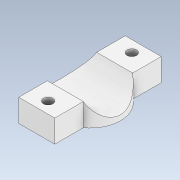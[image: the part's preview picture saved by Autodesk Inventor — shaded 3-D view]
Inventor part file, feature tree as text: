
AUTODESK INVENTOR PART (.ipt)
format: ipt  version: 2022 (Build 260153000, 153)  size: 269,312 bytes
history: native  units: mm
features: extrude x20, sketch x20, projected_geometry x15, plane x2
ambient origin geometry x8: Origin, YZ Plane, XZ Plane, XY Plane, X Axis, Y Axis, Z Axis, Center Point
bodies: Solid1 (feature_tree)
feature tree (57):
  extrude  "Extrusion1"  Depth=22.0mm
  extrude  "Extrusion2"  Depth=10.0mm
  extrude  "Extrusion3"  Depth=15.0mm
  extrude  "Extrusion4"  Depth=10.0mm TaperAngle=0.0deg
  extrude  "Extrusion5"  Depth=5.0mm
  extrude  "Extrusion6"  Depth=10.0mm
  plane  "Work Plane1"
  extrude  "Extrusion7"  Depth=29.0mm
  extrude  "Extrusion8"  TaperAngle=0.0deg  [1 undecoded]
  extrude  "Extrusion9"  Depth=10.0mm TaperAngle=0.0deg
  extrude  "Extrusion10"  TaperAngle=0.0deg  [1 undecoded]
  extrude  "Extrusion11"  Depth=10.0mm TaperAngle=0.0deg
  plane  "Work Plane2"
  extrude  "Extrusion12"  TaperAngle=0.0deg  [1 undecoded]
  extrude  "Extrusion13"  Depth=10.0mm TaperAngle=0.0deg
  extrude  "Extrusion14"  Depth=8.5mm
  extrude  "Extrusion15"  Depth=2.7mm TaperAngle=0.0deg
  extrude  "Extrusion16"  [1 undecoded]
  extrude  "Extrusion17"  [1 undecoded]
  extrude  "Extrusion18"  [1 undecoded]
  extrude  "Extrusion19"  [1 undecoded]
  extrude  "Extrusion20"  [1 undecoded]
  sketch  "Sketch1"  dims[d0=28.0mm d1=22.0mm]
  sketch  "Sketch2"  dims[d2=10.0mm d3=0.0mm d4=35.0mm]
  sketch  "Sketch3"  dims[d5=3.0mm d6=0.0mm d7=15.0mm]
  sketch  "Sketch4"  dims[d8=3.0mm d9=0.0mm d10=10.0mm d11=0.0mm]
  projected_geometry  "Projected Loop1"
  projected_geometry  "Projected Loop2"
  sketch  "Sketch5"  dims[d12=3.0mm d13=5.0mm]
  sketch  "Sketch6"  dims[d14=2.0mm d15=10.0mm]
  sketch  "Sketch7"  dims[d16=0.0mm d17=0.0mm d18=29.0mm]
  sketch  "Sketch8"  dims[d19=10.0mm d20=0.0mm d21=0.0mm d22=0.0mm]
  sketch  "Sketch9"  dims[d23=10.0mm d24=0.0mm d25=13.0mm d26=0.0mm]
  projected_geometry  "Projected Loop3"
  sketch  "Sketch10"  dims[d27=3.8mm d28=0.0mm d29=0.0mm d30=0.0mm]
  sketch  "Sketch11"  dims[d31=10.0mm d32=0.0mm d33=13.0mm d34=0.0mm]
  projected_geometry  "Projected Loop4"
  sketch  "Sketch12"  dims[d35=3.8mm d36=0.0mm d37=0.0mm d38=0.0mm]
  projected_geometry  "Projected Loop5"
  sketch  "Sketch13"  dims[d39=10.0mm d40=0.0mm d41=10.0mm d42=0.0mm]
  projected_geometry  "Projected Loop6"
  sketch  "Sketch14"  dims[d43=8.5mm d44=8.5mm]
  projected_geometry  "Projected Loop7"
  sketch  "Sketch15"  dims[d45=2.7mm d46=0.0mm d47=2.7mm d48=0.0mm]
  projected_geometry  "Projected Loop8"
  sketch  "Sketch16"  dims[d49=3.0mm d50=0.0mm]
  projected_geometry  "Projected Loop9"
  sketch  "Sketch17"
  projected_geometry  "Projected Loop10"
  projected_geometry  "Projected Loop11"
  sketch  "Sketch18"
  sketch  "Sketch19"
  projected_geometry  "Projected Loop12"
  projected_geometry  "Projected Loop13"
  sketch  "Sketch20"
  projected_geometry  "Projected Loop14"
  projected_geometry  "Projected Loop15"
note: 8 required parameter values undecoded (feature->parameter linkage not recoverable at this tier; creation-order binding heuristic only, values carry confidence <= 0.55)
